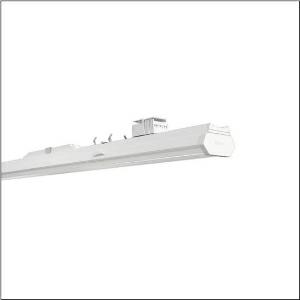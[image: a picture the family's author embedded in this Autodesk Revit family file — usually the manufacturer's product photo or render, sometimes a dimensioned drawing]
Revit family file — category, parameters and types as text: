
# Revit family: licross_r__11_protected_mo_51tp11cn58xf_4d9e
name_source: partatom
category: Lighting Fixtures
units: mm (PartAtom-declared; Revit-internal decimal feet)

## family parameters
Cut with Voids When Loaded = No
Host = Face
Light Source = No
Part Type = Normal
Room Calculation Point = No
Round Connector Dimension = Use Diameter
Shared = No

## types (1)
- --- (1 x LED, 8150 lm, 49 W, 5000K)
    Apparent Load = 49 VA
    CIE Flux Codes = 83 94 98 100 100
    Color Rendering = 80
    Color Temperature = 5000K
    Default Elevation = 1800 mm
    Description = Licross® 11 Protected MO, luminaire insert, of sheet steel, galvanised, coil coated, white, length: 1.500mm, width: 90mm, height: 101mm, LED rated luminous flux: 8.150lm, light colour: 850, control gear: ON/OFF Multilumen, CLOi, control gear: ECG Multilumen, with plug, 3-pole, with phase selection, mains connection: 220..240V, AC, 50/60Hz, start of lifetime: 49W, end of service life: 54W, halogen-free wiring, primary optical cover: cover, of PMMA, light emission: direct distribution, primary light characteristic: symmetric, protection rating (complete): IP64, insulation class (complete): insulation class I (protective earthing), certification: CE, ENEC, VDE, UKCA, protection symbol: D if used in an environment with conductive dust loads with corresponding accessories, impact resistance: IK06, permissible ambient temperature for indoor applications: -35..+40°C, corresponds to IFS (International Featured Standards) requirements for safety and quality in the food industry, reducing of maximum allowable ambient temperature of 5°C with ceiling mounting, LABS conformity tested according to VDMA 24364:2018-05, packaging unit: 1 piece
    Height = 92 mm
    Lamp = 1 x LED
    Lamp Light Flux = 8150 lm
    Lamp Power = 49 W
    Lamp count = 1
    Length = 1500 mm
    Luminous efficacy = 166 lm/W
    Manufacturer = Siteco
    ModVariant = No
    Model = 51TP11CN58XF
    Mounting Place = Ceiling
    Mounting Type = Pendant
    Number of Poles = 1
    OnlyDefault = Yes
    Power Factor = 1
    Product Name = Licross® 11 Protected MO
    Product group = luminaire insert
    ProductGroupID = 902
    Protection Class = Protection class I
    Protection Degree = IP 64
    RLX_Detail_Level = 1
    RLX_Emergency_Light_Flux = 0 lm
    RLX_Emergency_Type = 0
    RLX_Emergency_Type_DB = No
    RlxData = <blob elided: 21765 chars, md5=28ee35f2>
    Socket = socket
    Standby Power = 0 W
    System Light Flux = 8150 lm
    System Power = 49 W
    Type Comments = factory setting: luminous flux: 100 % | (A | C | E) | 111 mA
    Type Image = l_1256148.jpg
    URL = http://relux.com
    VarID = @adj_199854
    Voltage = 0 V
    Weight = 0.00 kg
    Width = 88 mm

## geometry (parser evidence)
native form markers: Blend x4, Sweep x12
no freeform markers — native parametric forms only
